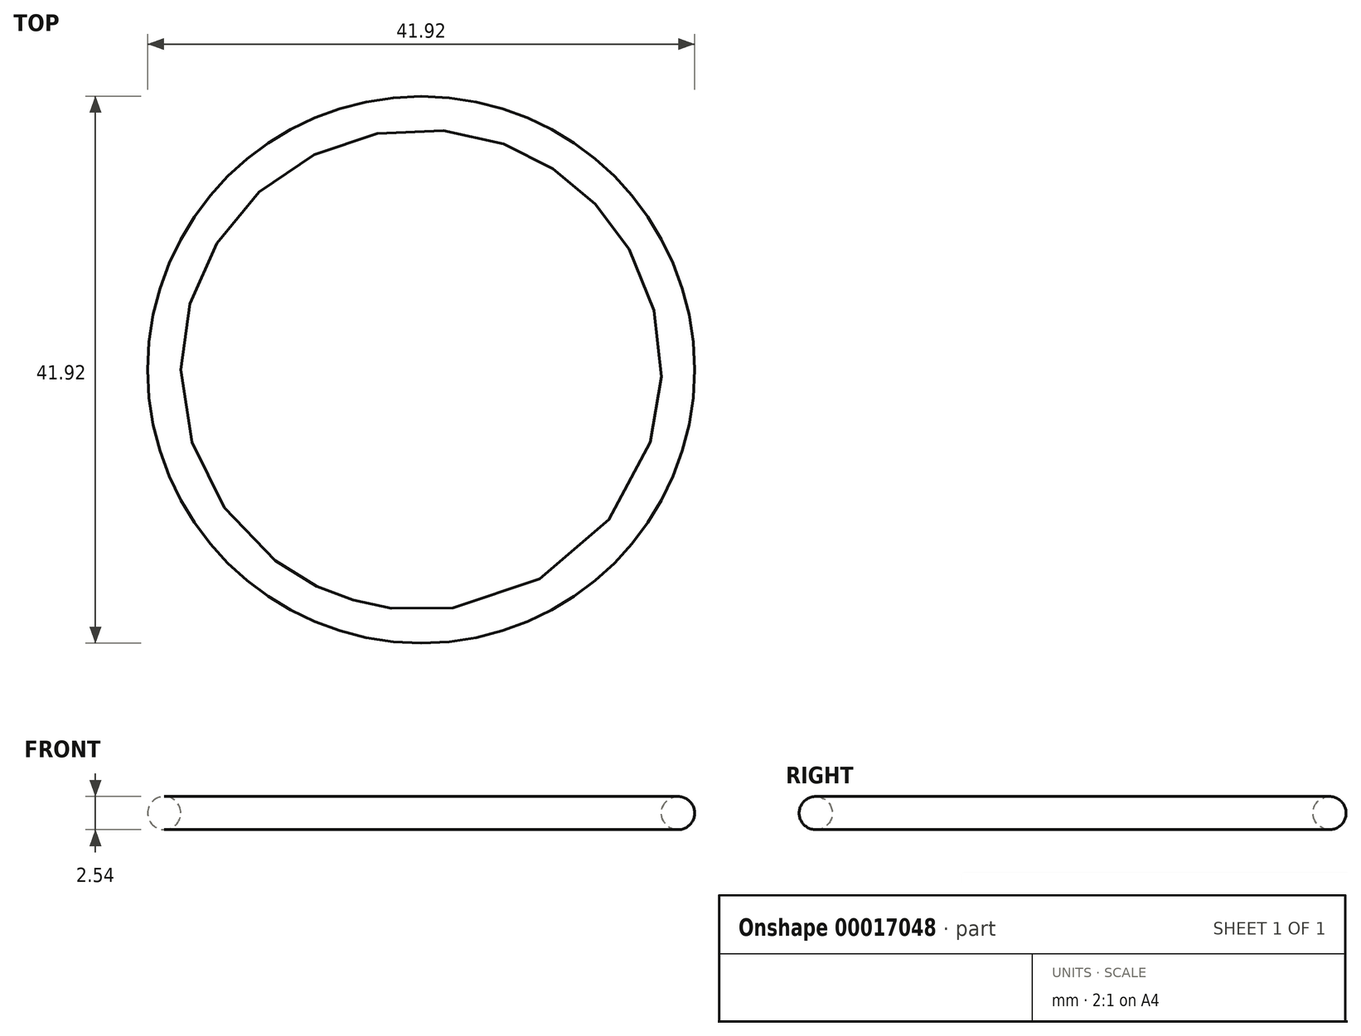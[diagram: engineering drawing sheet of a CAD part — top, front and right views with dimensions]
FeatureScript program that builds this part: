
annotation { "Feature Type Name" : "Feature", "Feature Type Description" : "" }
export const myFeature = defineFeature(function(context is Context, id is Id, definition is map)
    precondition{}
    {
        {
            var Q0;
            Q0=qCreatedBy(makeId("Top.planeOp"),FACE);
            var sketch = newSketch(context, id + "F0", { "sketchPlane" : qUnion([Q0])});
            skCircle(sketch, "E0", {"center": v(0, 0) * mm, "radius": 19.69 * mm});
            skSolve(sketch);
        }
        {
            var Q0;
            Q0=qCreatedBy(makeId("Front.planeOp"),FACE);
            var sketch = newSketch(context, id + "F1", { "sketchPlane" : qUnion([Q0])});
            skCircle(sketch, "E1", {"center": v(19.69, 0) * mm, "radius": 1.27 * mm});
            skSolve(sketch);
        }
        {
            var Q0;
            Q0=makeQuery(id+"F1.imprint","IMPRINT",FACE,{"disambiguationData":[TD([[makeQuery(id+"F1.imprint","IMPRINT",EDGE,{"derivedFrom":sQuery(id+"F1.wireOp",EDGE,"E1")}),1.0]])]});
            var Q1;
            Q1=sQuery(id+"F0.wireOp",EDGE,"E0");
            revolve(context, id + "F2", {"entities" : qUnion([Q0]), "axis" : qUnion([Q1]), "revolveType" : RevolveType.FULL});
        }
    });
